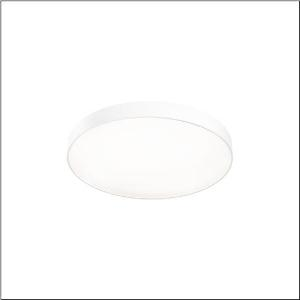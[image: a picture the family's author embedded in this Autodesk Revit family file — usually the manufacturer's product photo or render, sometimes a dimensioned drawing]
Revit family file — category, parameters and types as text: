
# Revit family: round_21_m_51mr36gm8421w
name_source: partatom
category: Lighting Fixtures
units: mm (PartAtom-declared; Revit-internal decimal feet)

## family parameters
Cut with Voids When Loaded = No
Host = Face
Light Source = No
Part Type = Normal
Room Calculation Point = No
Round Connector Dimension = Use Diameter
Shared = No

## types (1)
- --- (1 x LED, 8190 lm, 60.8 W, 4000K)
    Apparent Load = 61 VA
    CIE Flux Codes = 49 80 96 85 100
    Color Rendering = 80
    Color Temperature = 4000K
    Default Elevation = 1800 mm
    Description = Round 21 M, wall and ceiling luminaire, primary optical cover: cover, of PMMA, opal, light emission: direct/indirect distribution, primary light characteristic: symmetric, installation type: suspended mounting, surface-mounted, LED, rated luminous flux: 8.190lm, luminous efficacy: 135lm/W, light colour: 840, colour temperature: 4000K, with terminal, 3-pole, mains connection: 230V, AC, 50/60Hz, rated input power: 61W, housing, of aluminium, coated, white, diameter: 600mm, height: 62mm, protection rating (complete): IP40, insulation class (complete): insulation class I (protective earthing), certification: CE, impact resistance: IK04, permissible operating ambient temperature: -10..+35°C, packaging unit: 1 piece
    Height = 87 mm
    Lamp = 1 x LED
    Lamp Light Flux = 8190 lm
    Lamp Power = 60.8 W
    Lamp count = 1
    Length = 600 mm
    Luminous efficacy = 135 lm/W
    Manufacturer = Siteco
    ModVariant = No
    Model = 51MR36GM8421W
    Mounting Place = Ceiling
    Mounting Type = Surface mounted
    Number of Poles = 1
    OnlyDefault = Yes
    Power Factor = 1
    Product Name = Round 21 M
    Product group = wall and ceiling luminaire
    ProductGroupID = 302
    Protection Class = Protection class I
    Protection Degree = IP 40
    RLX_Detail_Level = 1
    RLX_Emergency_Light_Flux = 0 lm
    RLX_Emergency_Type = 0
    RLX_Emergency_Type_DB = No
    RlxData = <blob elided: 14761 chars, md5=36bebfb1>
    Socket = socket
    Standby Power = 0 W
    System Light Flux = 8190 lm
    System Power = 61 W
    Type Comments = factory setting: luminous flux: 100 % | (ON | ON | ON | ON) | 700 mA
    Type Image = l_1258330.jpg
    URL = http://relux.com
    VarID = @adj_031983
    Voltage = 0 V
    Weight = 0.00 kg
    Width = 0 mm  [stored 0 ft]

note: [stored X ft] marks values corroborated as IEEE doubles in the binary element streams (Revit-internal decimal feet)

## geometry (parser evidence)
native form markers: Sweep x12
no freeform markers — native parametric forms only
